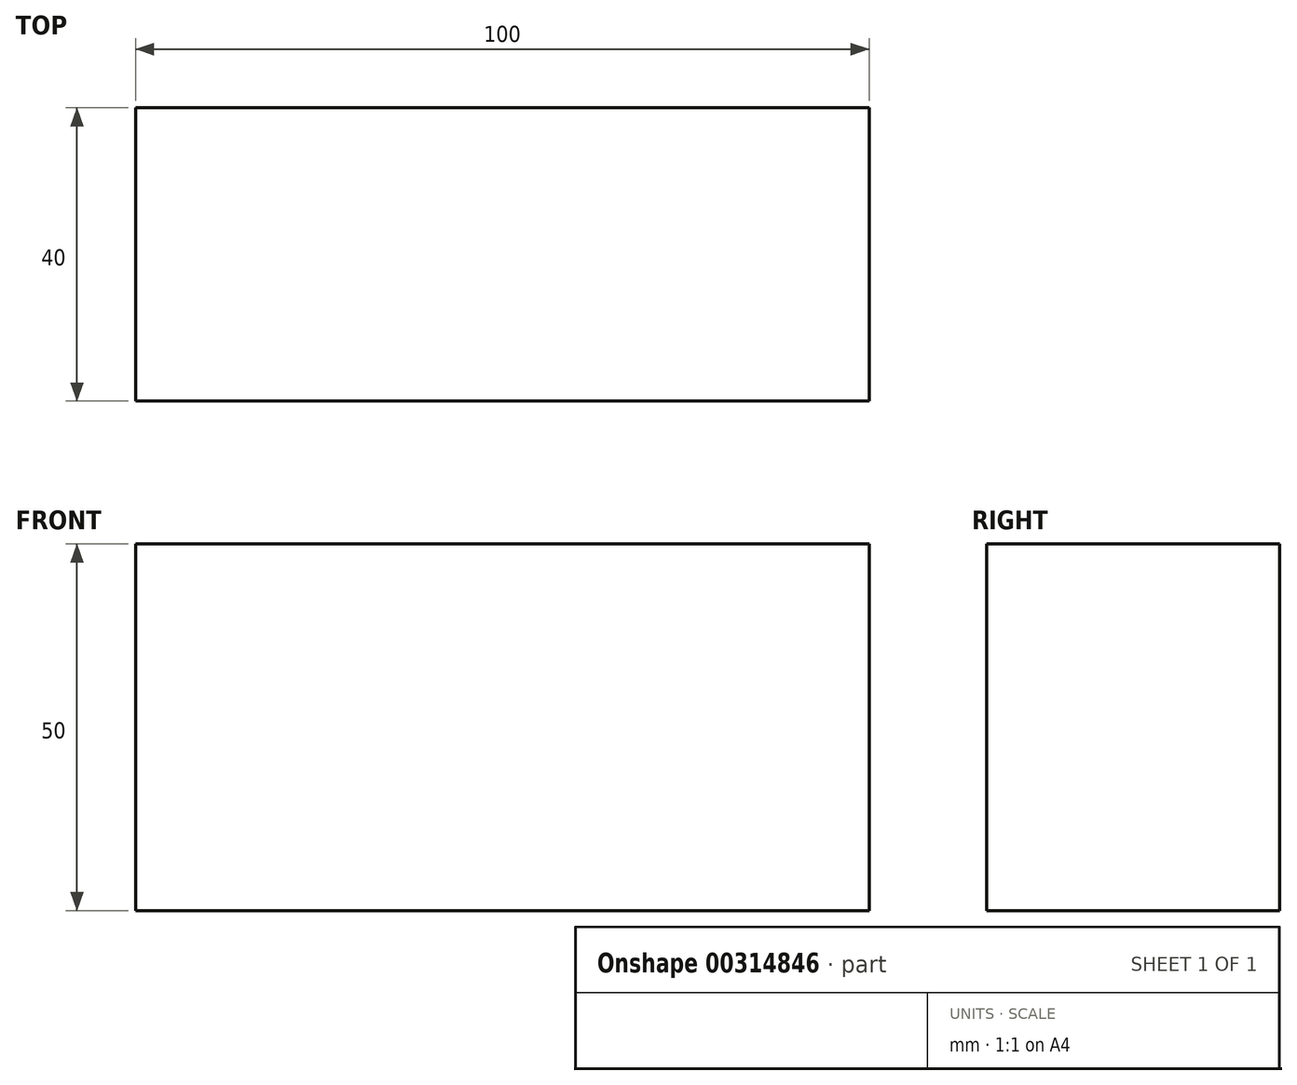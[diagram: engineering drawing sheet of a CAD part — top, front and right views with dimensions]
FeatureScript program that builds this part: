
annotation { "Feature Type Name" : "Feature", "Feature Type Description" : "" }
export const myFeature = defineFeature(function(context is Context, id is Id, definition is map)
    precondition{}
    {
        {
            var Q0;
            Q0=qCreatedBy(makeId("Front.planeOp"),FACE);
            var sketch = newSketch(context, id + "F0", { "sketchPlane" : qUnion([Q0])});
            skLineSegment(sketch, "E0.bottom", {"start": v(-50, 25) * mm, "end": v(50, 25) * mm});
            skLineSegment(sketch, "E0.top", {"start": v(-50, -25) * mm, "end": v(50, -25) * mm});
            skLineSegment(sketch, "E0.left", {"start": v(-50, 25) * mm, "end": v(-50, -25) * mm});
            skLineSegment(sketch, "E0.right", {"start": v(50, 25) * mm, "end": v(50, -25) * mm});
            skPoint(sketch, "E0.middle", {"position": v(0, 0) * mm});
            skSolve(sketch);
        }
        {
            var Q0;
            Q0=makeQuery(id+"F0.imprint","IMPRINT",FACE,{"disambiguationData":[TD([[makeQuery(id+"F0.imprint","IMPRINT",EDGE,{"derivedFrom":sQuery(id+"F0.wireOp",EDGE,"E0.bottom")}),-1.0]])]});
            extrude(context, id + "F1", {"entities" : qUnion([Q0]), "depth" : 40 * mm});
        }
    });
